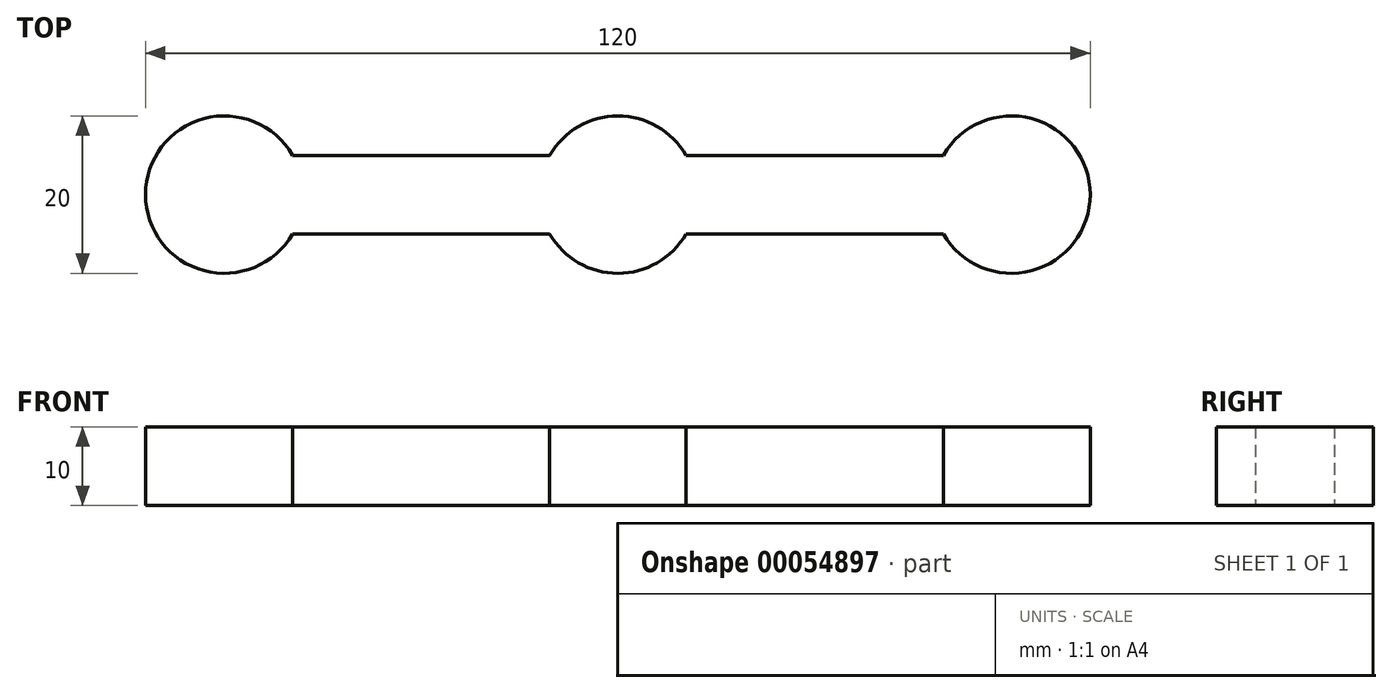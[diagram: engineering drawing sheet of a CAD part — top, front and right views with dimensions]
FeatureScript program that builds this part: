
annotation { "Feature Type Name" : "Feature", "Feature Type Description" : "" }
export const myFeature = defineFeature(function(context is Context, id is Id, definition is map)
    precondition{}
    {
        {
            var Q0;
            Q0=qCreatedBy(makeId("Top.planeOp"),FACE);
            var sketch = newSketch(context, id + "F0", { "sketchPlane" : qUnion([Q0])});
            skArc(sketch, "E0", {"start": v(8.66, 5) * mm, "mid": v(-10, 0) * mm, "end": v(8.66, -5) * mm});
            skArc(sketch, "E1", {"start": v(91.34, -5) * mm, "mid": v(110, 0) * mm, "end": v(91.34, 5) * mm});
            skLineSegment(sketch, "E2", {"start": v(0, 0) * mm, "end": v(100, 0) * mm, "construction": true});
            skLineSegment(sketch, "E3.0", {"start": v(8.66, -5) * mm, "end": v(41.34, -5) * mm});
            skLineSegment(sketch, "E4.0", {"start": v(8.66, 5) * mm, "end": v(41.34, 5) * mm});
            skArc(sketch, "E5", {"start": v(58.66, 5) * mm, "mid": v(50, 10) * mm, "end": v(41.34, 5) * mm});
            skLineSegment(sketch, "E6.trimOffspring", {"start": v(58.66, 5) * mm, "end": v(91.34, 5) * mm});
            skLineSegment(sketch, "E7.trimOffspring", {"start": v(58.66, -5) * mm, "end": v(91.34, -5) * mm});
            skArc(sketch, "E8.trimOffspring", {"start": v(41.34, -5) * mm, "mid": v(50, -10) * mm, "end": v(58.66, -5) * mm});
            skSolve(sketch);
        }
        {
            var Q0;
            Q0=qSketchRegion(id+"F0",true);
            extrude(context, id + "F1", {"entities" : qUnion([Q0]), "depth" : 10 * mm});
        }
    });
